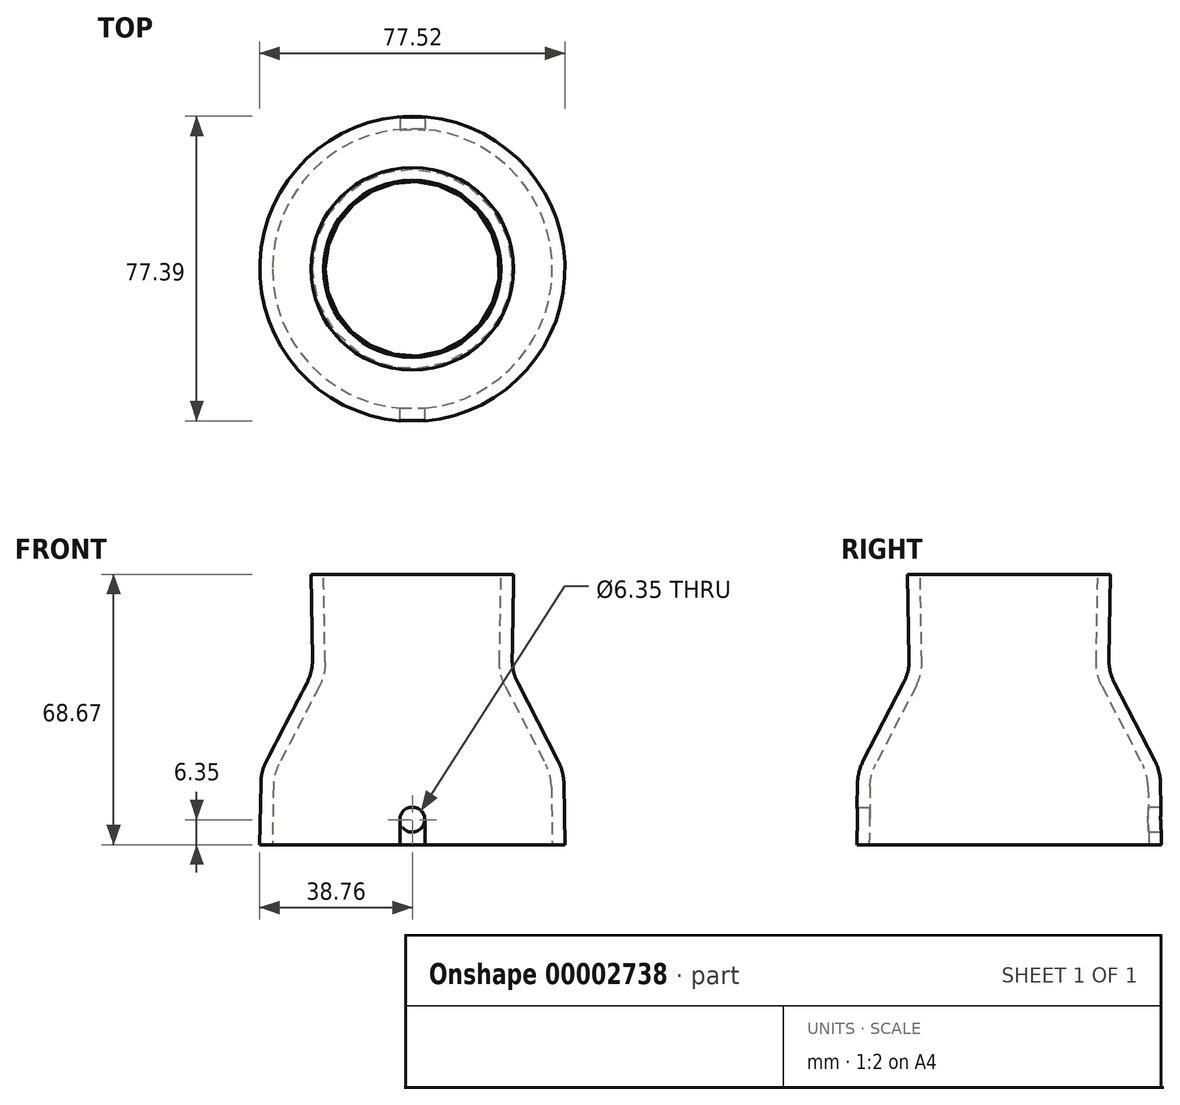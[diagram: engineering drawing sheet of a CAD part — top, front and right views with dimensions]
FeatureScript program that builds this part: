
annotation { "Feature Type Name" : "Feature", "Feature Type Description" : "" }
export const myFeature = defineFeature(function(context is Context, id is Id, definition is map)
    precondition{}
    {
        {
            var Q0;
            Q0=qCreatedBy(makeId("Front.planeOp"),FACE);
            var sketch = newSketch(context, id + "F0", { "sketchPlane" : qUnion([Q0])});
            skLineSegment(sketch, "E0", {"start": v(35.56, 0) * mm, "end": v(35.25, 17.78) * mm});
            skLineSegment(sketch, "E1", {"start": v(35.25, 17.78) * mm, "end": v(22.1, 43.18) * mm});
            skLineSegment(sketch, "E2", {"start": v(22.1, 43.18) * mm, "end": v(22.54, 68.58) * mm});
            skLineSegment(sketch, "E3", {"start": v(0, 0) * mm, "end": v(0, 58.65) * mm});
            skLineSegment(sketch, "E4", {"start": v(22.54, 68.58) * mm, "end": v(25.75, 68.67) * mm});
            skLineSegment(sketch, "E5", {"start": v(25.75, 68.67) * mm, "end": v(25.31, 43.93) * mm});
            skLineSegment(sketch, "E6", {"start": v(25.31, 43.93) * mm, "end": v(38.44, 18.59) * mm});
            skLineSegment(sketch, "E7", {"start": v(38.44, 18.59) * mm, "end": v(38.76, 0) * mm});
            skLineSegment(sketch, "E8", {"start": v(38.76, 0) * mm, "end": v(35.56, 0) * mm});
            skSolve(sketch);
        }
        {
            var Q0;
            Q0=makeQuery(id+"F0.imprint","IMPRINT",FACE,{"disambiguationData":[TD([[makeQuery(id+"F0.imprint","IMPRINT",EDGE,{"derivedFrom":sQuery(id+"F0.wireOp",EDGE,"E0")}),-1.0]])]});
            var Q1;
            Q1=sQuery(id+"F0.wireOp",EDGE,"E1");
            var Q2;
            Q2=sQuery(id+"F0.wireOp",EDGE,"E6");
            var Q3;
            Q3=sQuery(id+"F0.wireOp",EDGE,"E7");
            var Q4;
            Q4=sQuery(id+"F0.wireOp",EDGE,"E5");
            var Q5;
            Q5=sQuery(id+"F0.wireOp",EDGE,"E0");
            var Q6;
            Q6=sQuery(id+"F0.wireOp",EDGE,"E2");
            var Q7;
            Q7=sQuery(id+"F0.wireOp",EDGE,"E4");
            var Q8;
            Q8=sQuery(id+"F0.wireOp",EDGE,"E8");
            var Q9;
            Q9=sQuery(id+"F0.wireOp",EDGE,"E3");
            revolve(context, id + "F1", {"entities" : qUnion([Q0]), "surfaceEntities" : qUnion([Q1, Q2, Q3, Q4, Q5, Q6, Q7, Q8]), "axis" : qUnion([Q9]), "revolveType" : RevolveType.FULL});
        }
        {
            var Q0;
            Q0=qCreatedBy(makeId("Front.planeOp"),FACE);
            var sketch = newSketch(context, id + "F2", { "sketchPlane" : qUnion([Q0])});
            skCircle(sketch, "E9", {"center": v(0, 6.35) * mm, "radius": 3.18 * mm});
            skLineSegment(sketch, "E10", {"start": v(-3.17, 6.34) * mm, "end": v(-3.15, 0) * mm});
            skLineSegment(sketch, "E11", {"start": v(3.18, 6.35) * mm, "end": v(3.18, 0) * mm});
            skLineSegment(sketch, "E12", {"start": v(-3.15, 0) * mm, "end": v(3.18, 0) * mm});
            skSolve(sketch);
        }
        {
            var Q0;
            Q0=makeQuery(id+"F2.imprint","IMPRINT",FACE,{"disambiguationData":[TD([[makeQuery(id+"F2.imprint","IMPRINT",EDGE,{"derivedFrom":sQuery(id+"F2.wireOp",EDGE,"E9")}),1.0]])]});
            var Q1;
            Q1=sQuery(id+"F2.wireOp",EDGE,"E9");
            extrude(context, id + "F3", {"entities" : qUnion([Q0]), "operationType" : NewBodyOperationType.REMOVE, "surfaceEntities" : qUnion([Q1]), "endBound" : BoundingType.THROUGH_ALL, "oppositeDirection" : true, "depth" : 25.4 * mm});
        }
        {
            var Q0;
            {var subQ1=sQuery(id+"F2.wireOp",EDGE,"E10");Q0=makeQuery(id+"F2.imprint","IMPRINT",FACE,{"disambiguationData":[TD([[makeQuery(id+"F2.imprint","IMPRINT",EDGE,{"derivedFrom":subQ1}),1.0]])]});}
            var Q1;
            {var subQ0=sQuery(id+"F2.wireOp",EDGE,"E9");var subQ2=makeQuery(id+"F2.imprint","INTERSECT",VERTEX,{"derivedFrom":[subQ0,sQuery(id+"F2.wireOp",EDGE,"E10")]});Q1=makeQuery(id+"F2.imprint","IMPRINT",FACE,{"disambiguationData":[TD([[makeQuery(id+"F2.imprint","IMPRINT",EDGE,{"disambiguationData":[TD([[subQ2,1.0]])],"derivedFrom":subQ0}),1.0]])]});}
            extrude(context, id + "F4", {"entities" : qUnion([Q0, Q1]), "operationType" : NewBodyOperationType.REMOVE, "endBound" : BoundingType.THROUGH_ALL, "depth" : 25.4 * mm});
        }
        {
            var Q0;
            Q0=makeQuery(id+"F1.opRevolve","SWEPT_EDGE",EDGE,{"disambiguationData":[OSD([sQuery(id+"F0.wireOp",EDGE,"E1"),sQuery(id+"F0.wireOp",EDGE,"E2")])]});
            var Q1;
            Q1=makeQuery(id+"F1.opRevolve","SWEPT_EDGE",EDGE,{"disambiguationData":[OSD([sQuery(id+"F0.wireOp",EDGE,"E5"),sQuery(id+"F0.wireOp",EDGE,"E6")])]});
            var Q2;
            Q2=makeQuery(id+"F1.opRevolve","SWEPT_EDGE",EDGE,{"disambiguationData":[OSD([sQuery(id+"F0.wireOp",EDGE,"E6"),sQuery(id+"F0.wireOp",EDGE,"E7")])]});
            var Q3;
            Q3=makeQuery(id+"F1.opRevolve","SWEPT_EDGE",EDGE,{"disambiguationData":[OSD([sQuery(id+"F0.wireOp",EDGE,"E0"),sQuery(id+"F0.wireOp",EDGE,"E1")])]});
            fillet(context, id + "F5", {"entities" : qUnion([Q0, Q1, Q2, Q3]), "radius" : 12.7 * mm, "tangentPropagation" : true, "allowEdgeOverflow" : false});
        }
    });
